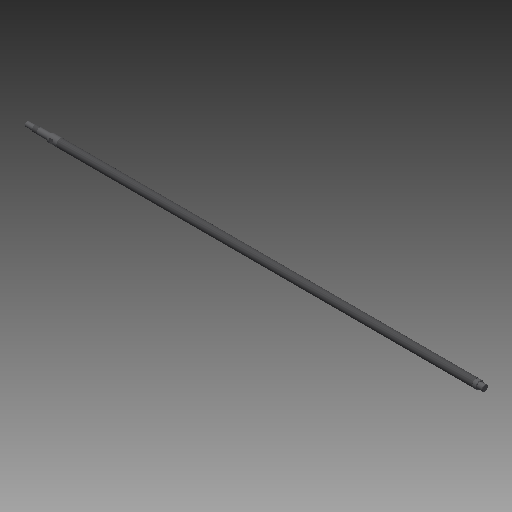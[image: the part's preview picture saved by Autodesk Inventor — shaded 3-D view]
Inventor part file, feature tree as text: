
AUTODESK INVENTOR PART (.ipt)
format: ipt  version: 2018 (Build 220112000, 112)  size: 145,920 bytes
history: native  units: mm
features: other x21, sketch x5, revolve x3, thread x2, extrude x2
ambient origin geometry x8: Origin, YZ Plane, XZ Plane, XY Plane, X Axis, Y Axis, Z Axis, Center Point
bodies: Solid1 (feature_tree)
feature tree (33):
  revolve  "Revolution1"  [1 undecoded]
  thread  "Thread1"  [1 undecoded]
  revolve  "Revolution2"  [1 undecoded]
  thread  "Thread2"  [1 undecoded]
  extrude  "Extrusion1"  TaperAngle=0.0deg  [1 undecoded]
  extrude  "Extrusion2"  [1 undecoded]
  revolve  "Revolution3"  [1 undecoded]
  other  "FSS_XY"
  other  "FSS_YZ"
  other  "FSS_ZX"
  other  "FSS_X"
  other  "FSS_Y"
  other  "FSS_Z"
  other  "FSS_Center"
  other  "SSS_XY"
  other  "SSS_YZ"
  other  "SSS_ZX"
  other  "SSS_X"
  other  "SSS_Y"
  other  "SSS_Z"
  other  "SSS_Center"
  other  "bnt_s_1_XY"
  other  "bnt_s_1_YZ"
  other  "bnt_s_1_ZX"
  other  "bnt_s_1_X"
  other  "bnt_s_1_Y"
  other  "bnt_s_1_Z"
  other  "bnt_s_1_Center"
  sketch  "Sketch_1"  dims[d0=360.0deg d1=1058.0mm d2=0.0mm d3=360.0deg]
  sketch  "Sketch_10"  dims[d4=11.3865mm d5=0.0mm d6=4.0mm d7=0.0mm d8=4.0mm d9=0.0mm]
  sketch  "Sketch_11"  dims[d10=360.0deg d11=0.0mm d12=0.0mm d13=0.0mm]
  sketch  "Sketch_12"
  sketch  "Sketch_16"
note: 7 required parameter values undecoded (feature->parameter linkage not recoverable at this tier; creation-order binding heuristic only, values carry confidence <= 0.55)